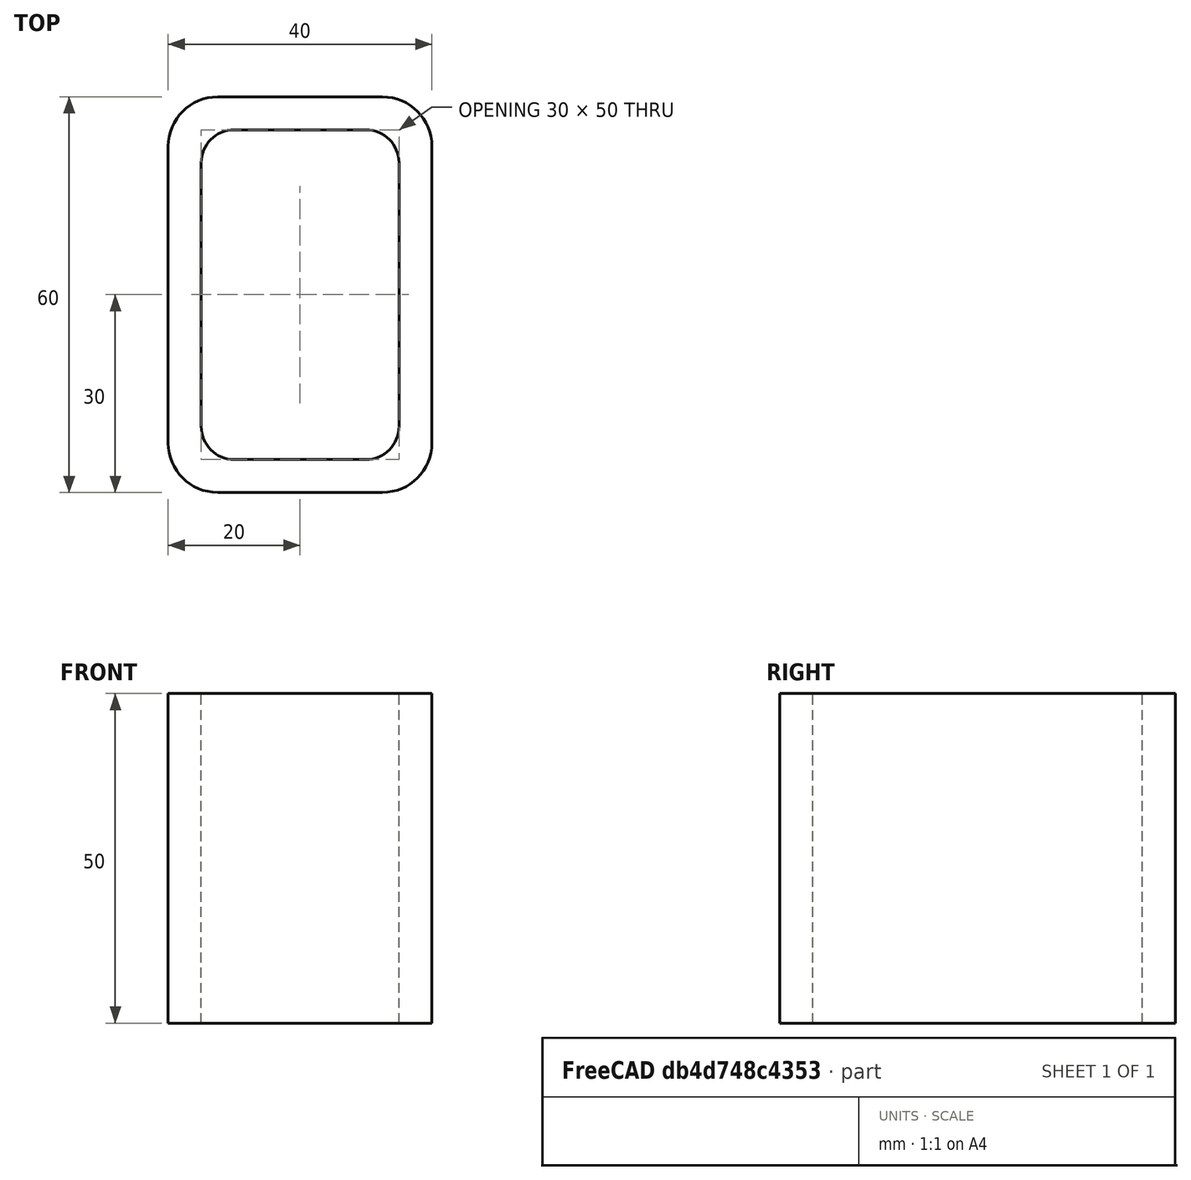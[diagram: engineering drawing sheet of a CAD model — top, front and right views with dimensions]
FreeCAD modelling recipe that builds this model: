
FCSTD DOCUMENT  (FreeCAD 0.15R4671 (Git))
Label: Rectangular hollow section 60x40x5 EN10219 S235JRH
License: All rights reserved
LicenseURL: http://en.wikipedia.org/wiki/All_rights_reserved
objects: Sketcher::SketchObject×1, Part::Extrusion×1
note: 2 computed .brp shape members not serialized (recipe doc carries the construction recipe); baked Part::Feature solids carry a one-line shape summary decoded from their .brp

FEATURE [Sketcher::SketchObject] Sketch
  sketch-geometry (16):
    g0: LineSegment StartX=-10 StartY=25 StartZ=0 EndX=10 EndY=25 EndZ=0
    g1: LineSegment StartX=15 StartY=20 StartZ=0 EndX=15 EndY=-20 EndZ=0
    g2: LineSegment StartX=10 StartY=-25 StartZ=0 EndX=-10 EndY=-25 EndZ=0
    g3: LineSegment StartX=-15 StartY=-20 StartZ=0 EndX=-15 EndY=20 EndZ=0
    g4: LineSegment StartX=-12.5 StartY=30 StartZ=0 EndX=12.5 EndY=30 EndZ=0
    g5: LineSegment StartX=20 StartY=22.5 StartZ=0 EndX=20 EndY=-22.5 EndZ=0
    g6: LineSegment StartX=12.5 StartY=-30 StartZ=0 EndX=-12.5 EndY=-30 EndZ=0
    g7: LineSegment StartX=-20 StartY=-22.5 StartZ=0 EndX=-20 EndY=22.5 EndZ=0
    g8: ArcOfCircle CenterX=-10 CenterY=20 CenterZ=0 NormalX=0 NormalY=0 NormalZ=1 Radius=5 StartAngle=1.5708 EndAngle=3.14159
    g9: ArcOfCircle CenterX=10 CenterY=20 CenterZ=0 NormalX=0 NormalY=0 NormalZ=1 Radius=5 StartAngle=0 EndAngle=1.5708
    g10: ArcOfCircle CenterX=10 CenterY=-20 CenterZ=0 NormalX=0 NormalY=0 NormalZ=1 Radius=5 StartAngle=4.71239 EndAngle=6.28319
    g11: ArcOfCircle CenterX=-10 CenterY=-20 CenterZ=0 NormalX=0 NormalY=0 NormalZ=1 Radius=5 StartAngle=3.14159 EndAngle=4.71239
    g12: ArcOfCircle CenterX=12.5 CenterY=22.5 CenterZ=0 NormalX=0 NormalY=0 NormalZ=1 Radius=7.5 StartAngle=0 EndAngle=1.5708
    g13: ArcOfCircle CenterX=12.5 CenterY=-22.5 CenterZ=0 NormalX=0 NormalY=0 NormalZ=1 Radius=7.5 StartAngle=4.71239 EndAngle=6.28319
    g14: ArcOfCircle CenterX=-12.5 CenterY=-22.5 CenterZ=0 NormalX=0 NormalY=0 NormalZ=1 Radius=7.5 StartAngle=3.14159 EndAngle=4.71239
    g15: ArcOfCircle CenterX=-12.5 CenterY=22.5 CenterZ=0 NormalX=0 NormalY=0 NormalZ=1 Radius=7.5 StartAngle=1.5708 EndAngle=3.14159
  constraints (36):
    c: Horizontal(g2)
    c: Vertical(g3)
    c: Horizontal(g6)
    c: Vertical(g7)
    c: Tangent(g3,g8) = 1.5708
    c: Tangent(g0,g8) = 1.5708
    c: Tangent(g0,g9) = 1.5708
    c: Tangent(g1,g9) = 1.5708
    c: Tangent(g1,g10) = 1.5708
    c: Tangent(g2,g10) = 1.5708
    c: Tangent(g2,g11) = 1.5708
    c: Tangent(g3,g11) = 1.5708
    c: Tangent(g4,g12) = 1.5708
    c: Tangent(g5,g12) = 1.5708
    c: Tangent(g5,g13) = 1.5708
    c: Tangent(g6,g13) = 1.5708
    c: Tangent(g6,g14) = 1.5708
    c: Tangent(g7,g14) = 1.5708
    c: Tangent(g7,g15) = 1.5708
    c: Tangent(g4,g15) = 1.5708
    c: Equal(g9,g8)
    c: Equal(g9,g11)
    c: Equal(g9,g10)
    c: Equal(g12,g15)
    c: Equal(g12,g14)
    c: Equal(g12,g13)
    c: Symmetric(g4,g6,g-1)
    c: Symmetric(g7,g5,g-2)
    c: DistanceY(g4,g6) = -60
    c: DistanceX(g7,g5) = 40
    c: Symmetric(g3,g1,g-2)
    c: Symmetric(g0,g2,g-1)
    c: DistanceY(g0,g4) = 5
    c: DistanceX(g5,g1) = -5
    c: Radius(g9) = 5
    c: Radius(g12) = 7.5
FEATURE [Part::Extrusion] Extrude  label="Rectangular hollow section 60x40x5 EN10219 S235JRH"
  Base = -> Sketch
  Dir = (0,0,50)
  Solid = true
